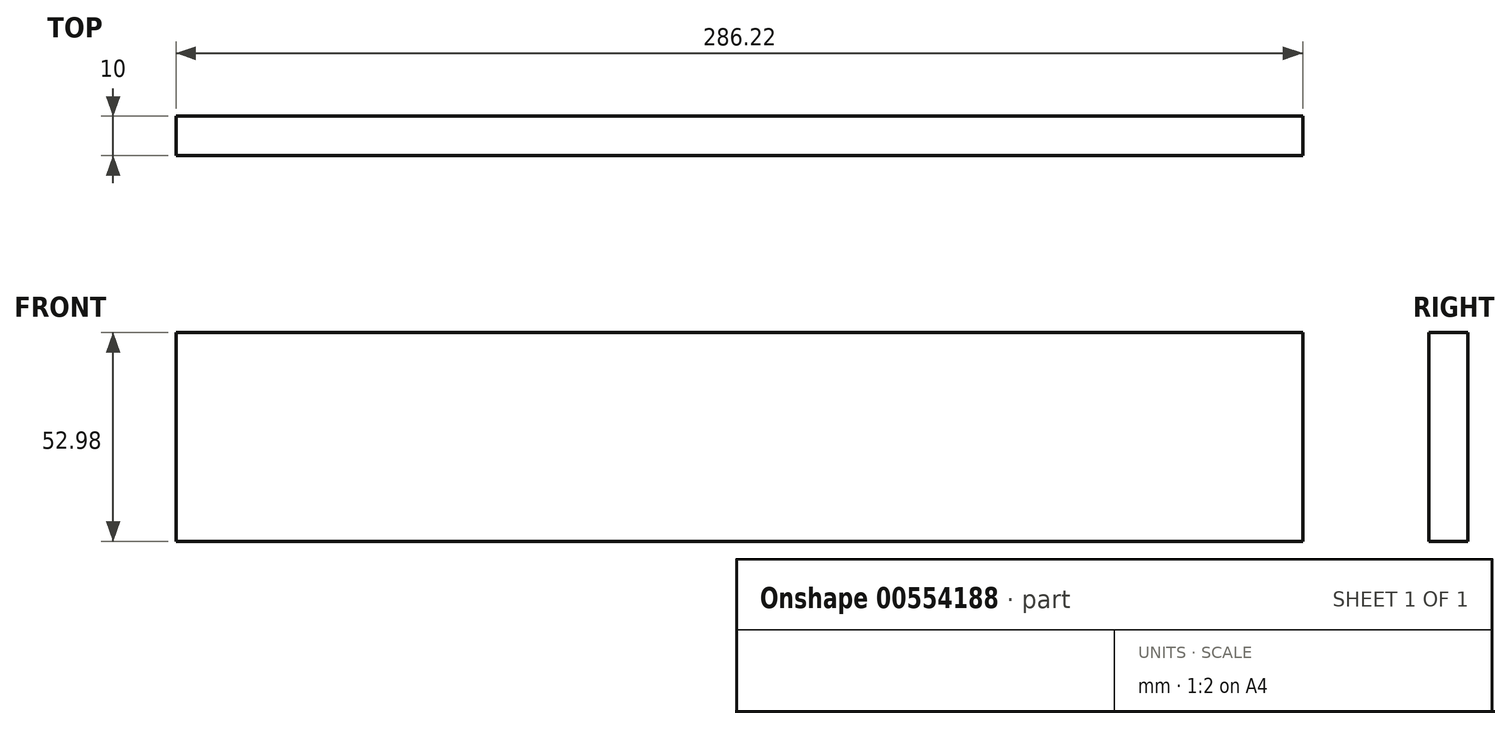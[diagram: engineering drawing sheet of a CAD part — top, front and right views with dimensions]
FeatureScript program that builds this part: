
annotation { "Feature Type Name" : "Feature", "Feature Type Description" : "" }
export const myFeature = defineFeature(function(context is Context, id is Id, definition is map)
    precondition{}
    {
        {
            var Q0;
            Q0=qCreatedBy(makeId("Front.planeOp"),FACE);
            var sketch = newSketch(context, id + "F0", { "sketchPlane" : qUnion([Q0])});
            skLineSegment(sketch, "E0", {"start": v(-144.7, 50.17) * mm, "end": v(-144.7, 0) * mm});
            skLineSegment(sketch, "E1", {"start": v(-144.7, 0) * mm, "end": v(141.53, 0) * mm});
            skLineSegment(sketch, "E2", {"start": v(141.53, 0) * mm, "end": v(141.53, 52.98) * mm});
            skLineSegment(sketch, "E3", {"start": v(141.53, 52.98) * mm, "end": v(-144.7, 52.98) * mm});
            skLineSegment(sketch, "E4", {"start": v(-144.7, 52.98) * mm, "end": v(-144.7, 50.17) * mm});
            skSolve(sketch);
        }
        {
            var Q0;
            Q0=makeQuery(id+"F0.imprint","IMPRINT",FACE,{"disambiguationData":[TD([[makeQuery(id+"F0.imprint","IMPRINT",EDGE,{"derivedFrom":sQuery(id+"F0.wireOp",EDGE,"E0")}),1.0]])]});
            var sketch = newSketch(context, id + "F1", { "sketchPlane" : qUnion([Q0])});
            skLineSegment(sketch, "E5", {"start": v(-144, 52.6) * mm, "end": v(-134, 52.6) * mm});
            skLineSegment(sketch, "E6", {"start": v(-134, 52.6) * mm, "end": v(-134, 0) * mm});
            skLineSegment(sketch, "E7", {"start": v(-134, 0) * mm, "end": v(-124, 0) * mm});
            skLineSegment(sketch, "E8", {"start": v(-124, 0) * mm, "end": v(-124, 52.6) * mm});
            skLineSegment(sketch, "E9", {"start": v(-124, 52.6) * mm, "end": v(-114, 52.6) * mm});
            skLineSegment(sketch, "E10", {"start": v(-114, 52.6) * mm, "end": v(-114, 0) * mm});
            skLineSegment(sketch, "E11", {"start": v(-114, 0) * mm, "end": v(-104, 0) * mm});
            skLineSegment(sketch, "E12", {"start": v(-104, 0) * mm, "end": v(-104, 52.6) * mm});
            skLineSegment(sketch, "E13", {"start": v(-104, 52.6) * mm, "end": v(-94, 52.6) * mm});
            skLineSegment(sketch, "E14", {"start": v(-94, 52.6) * mm, "end": v(-94, 0) * mm});
            skLineSegment(sketch, "E15", {"start": v(-94, 0) * mm, "end": v(-84, 0) * mm});
            skLineSegment(sketch, "E16", {"start": v(-84, 0) * mm, "end": v(-84, 52.6) * mm});
            skLineSegment(sketch, "E17", {"start": v(-84, 52.6) * mm, "end": v(-74, 52.6) * mm});
            skLineSegment(sketch, "E18", {"start": v(-74, 52.6) * mm, "end": v(-74, 0) * mm});
            skLineSegment(sketch, "E19", {"start": v(-74, 0) * mm, "end": v(-64, 0) * mm});
            skLineSegment(sketch, "E20", {"start": v(-64, 0) * mm, "end": v(-64, 52.6) * mm});
            skLineSegment(sketch, "E21", {"start": v(-64, 52.6) * mm, "end": v(-54, 52.6) * mm});
            skLineSegment(sketch, "E22", {"start": v(-54, 52.6) * mm, "end": v(-54, 0) * mm});
            skLineSegment(sketch, "E23", {"start": v(-54, 0) * mm, "end": v(-44, 0) * mm});
            skLineSegment(sketch, "E24", {"start": v(-44, 0) * mm, "end": v(-44, 52.6) * mm});
            skLineSegment(sketch, "E25", {"start": v(-44, 52.6) * mm, "end": v(-34, 52.6) * mm});
            skLineSegment(sketch, "E26", {"start": v(-34, 52.6) * mm, "end": v(-34, 0) * mm});
            skLineSegment(sketch, "E27", {"start": v(-34, 0) * mm, "end": v(-24, 0) * mm});
            skLineSegment(sketch, "E28", {"start": v(-24, 0) * mm, "end": v(-24, 52.6) * mm});
            skLineSegment(sketch, "E29", {"start": v(-24, 52.6) * mm, "end": v(-14, 52.6) * mm});
            skLineSegment(sketch, "E30", {"start": v(-14, 52.6) * mm, "end": v(-14, 0) * mm});
            skLineSegment(sketch, "E31", {"start": v(-14, 0) * mm, "end": v(-4, 0) * mm});
            skLineSegment(sketch, "E32", {"start": v(-4, 0) * mm, "end": v(-4, 52.6) * mm});
            skLineSegment(sketch, "E33", {"start": v(-4, 52.6) * mm, "end": v(6, 52.6) * mm});
            skLineSegment(sketch, "E34", {"start": v(6, 52.6) * mm, "end": v(6, 0) * mm});
            skLineSegment(sketch, "E35", {"start": v(6, 0) * mm, "end": v(16, 0) * mm});
            skLineSegment(sketch, "E36", {"start": v(16, 0) * mm, "end": v(16, 52.6) * mm});
            skLineSegment(sketch, "E37", {"start": v(16, 52.6) * mm, "end": v(26, 52.6) * mm});
            skLineSegment(sketch, "E38", {"start": v(26, 52.6) * mm, "end": v(26, 0) * mm});
            skLineSegment(sketch, "E39", {"start": v(26, 0) * mm, "end": v(36, 0) * mm});
            skLineSegment(sketch, "E40", {"start": v(36, 0) * mm, "end": v(36, 52.6) * mm});
            skLineSegment(sketch, "E41", {"start": v(36, 52.6) * mm, "end": v(46, 52.6) * mm});
            skLineSegment(sketch, "E42", {"start": v(46, 52.6) * mm, "end": v(46, 0) * mm});
            skLineSegment(sketch, "E43", {"start": v(46, 0) * mm, "end": v(56, 0) * mm});
            skLineSegment(sketch, "E44", {"start": v(56, 0) * mm, "end": v(56, 52.6) * mm});
            skLineSegment(sketch, "E45", {"start": v(56, 52.6) * mm, "end": v(66, 52.6) * mm});
            skLineSegment(sketch, "E46", {"start": v(66, 52.6) * mm, "end": v(66, 0) * mm});
            skLineSegment(sketch, "E47", {"start": v(66, 0) * mm, "end": v(76, 0) * mm});
            skLineSegment(sketch, "E48", {"start": v(76, 0) * mm, "end": v(76, 52.6) * mm});
            skLineSegment(sketch, "E49", {"start": v(76, 52.6) * mm, "end": v(86, 52.6) * mm});
            skLineSegment(sketch, "E50", {"start": v(86, 52.6) * mm, "end": v(86, 0) * mm});
            skLineSegment(sketch, "E51", {"start": v(86, 0) * mm, "end": v(96, 0) * mm});
            skLineSegment(sketch, "E52", {"start": v(96, 0) * mm, "end": v(96, 52.6) * mm});
            skSolve(sketch);
        }
        {
            var Q0;
            Q0=makeQuery(id+"F0.imprint","IMPRINT",FACE,{"disambiguationData":[TD([[makeQuery(id+"F0.imprint","IMPRINT",EDGE,{"derivedFrom":sQuery(id+"F0.wireOp",EDGE,"E0")}),1.0]])]});
            extrude(context, id + "F2", {"entities" : qUnion([Q0]), "depth" : 10 * mm, "offsetDistance" : 25 * mm});
        }
        {
            var Q0;
            {var subQ0=sQuery(id+"F1.wireOp",EDGE,"E48");Q0=makeQuery(id+"F1.imprint","IMPRINT",FACE,{"disambiguationData":[TD([[makeQuery(id+"F1.imprint","IMPRINT",EDGE,{"derivedFrom":subQ0}),-1.0]])]});}
            extrude(context, id + "F3", {"entities" : qUnion([Q0]), "operationType" : NewBodyOperationType.ADD, "depth" : 5 * mm, "offsetDistance" : 25 * mm});
        }
    });
